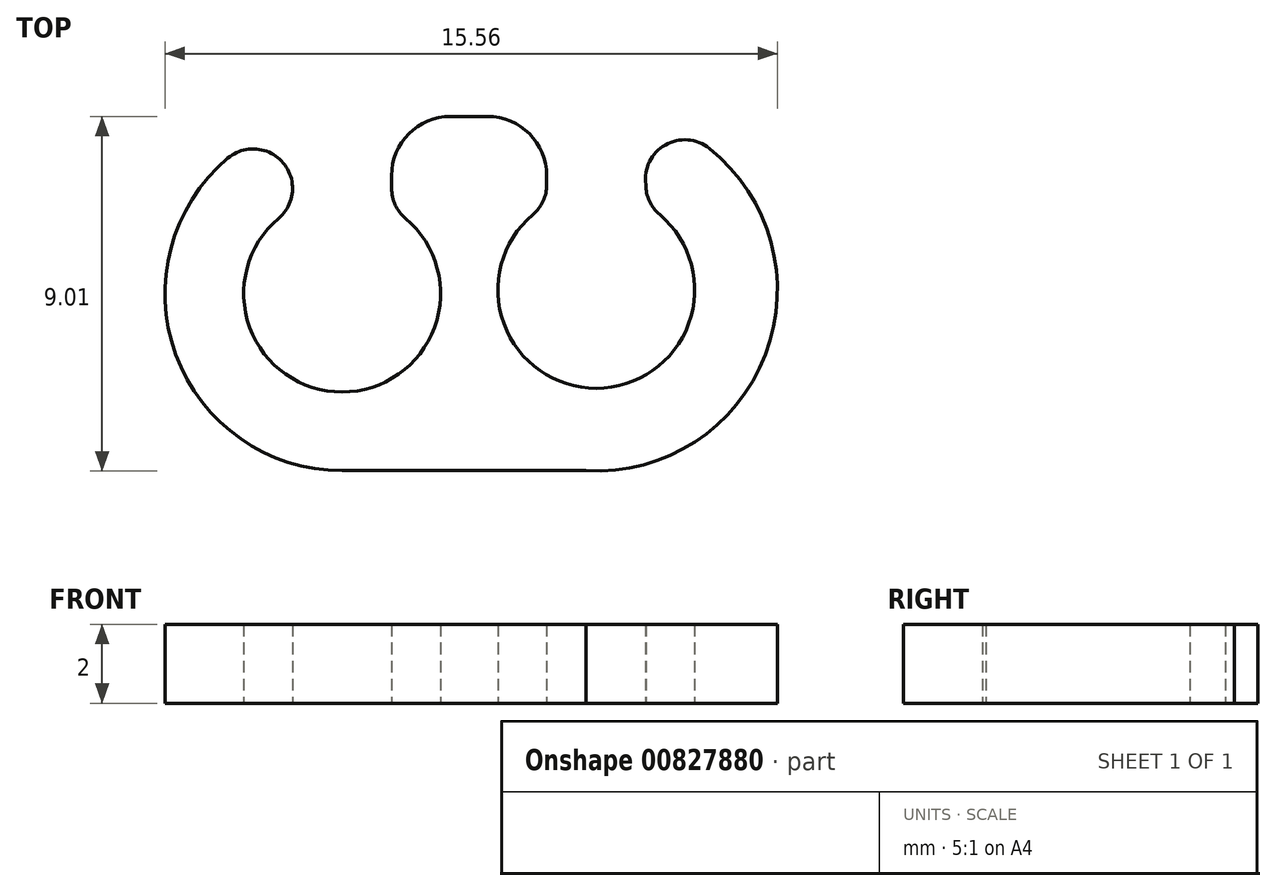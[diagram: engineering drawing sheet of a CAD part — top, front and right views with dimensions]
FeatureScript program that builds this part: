
annotation { "Feature Type Name" : "Feature", "Feature Type Description" : "" }
export const myFeature = defineFeature(function(context is Context, id is Id, definition is map)
    precondition{}
    {
        {
            var Q0;
            Q0=qCreatedBy(makeId("Top.planeOp"),FACE);
            var sketch = newSketch(context, id + "F0", { "sketchPlane" : qUnion([Q0])});
            skArc(sketch, "E0", {"start": v(-38.87, -11.61) * mm, "mid": v(-37.26, -16.02) * mm, "end": v(-35.65, -11.61) * mm});
            skArc(sketch, "E1.3.0.0", {"start": v(-32.41, -11.52) * mm, "mid": v(-30.8, -15.93) * mm, "end": v(-29.19, -11.52) * mm});
            skArc(sketch, "E2", {"start": v(-31.06, -18.02) * mm, "mid": v(-26.5, -15.07) * mm, "end": v(-27.93, -9.83) * mm});
            skArc(sketch, "E3", {"start": v(-40.16, -10.08) * mm, "mid": v(-41.49, -15.07) * mm, "end": v(-37.26, -18.02) * mm});
            skLineSegment(sketch, "E4", {"start": v(-34.5, -9.02) * mm, "end": v(-33.56, -9.02) * mm});
            skLineSegment(sketch, "E5.left", {"start": v(-36, -10.85) * mm, "end": v(-36, -10.52) * mm});
            skLineSegment(sketch, "E6.3.0.1", {"start": v(-32.06, -10.75) * mm, "end": v(-32.06, -10.52) * mm});
            skArc(sketch, "E7.filletArc", {"start": v(-38.87, -11.61) * mm, "mid": v(-38.61, -11.27) * mm, "end": v(-38.52, -10.85) * mm});
            skArc(sketch, "E8.filletArc", {"start": v(-36, -10.85) * mm, "mid": v(-35.9, -11.27) * mm, "end": v(-35.65, -11.61) * mm});
            skArc(sketch, "E9.filletArc", {"start": v(-38.52, -10.85) * mm, "mid": v(-39.1, -9.94) * mm, "end": v(-40.16, -10.08) * mm});
            skArc(sketch, "E10.filletArc", {"start": v(-27.93, -9.83) * mm, "mid": v(-29.05, -9.75) * mm, "end": v(-29.54, -10.75) * mm});
            skArc(sketch, "E11.filletArc", {"start": v(-29.54, -10.75) * mm, "mid": v(-29.45, -11.18) * mm, "end": v(-29.19, -11.52) * mm});
            skArc(sketch, "E12.filletArc", {"start": v(-32.41, -11.52) * mm, "mid": v(-32.15, -11.18) * mm, "end": v(-32.06, -10.75) * mm});
            skArc(sketch, "E13.filletArc", {"start": v(-34.5, -9.02) * mm, "mid": v(-35.56, -9.46) * mm, "end": v(-36, -10.52) * mm});
            skArc(sketch, "E14.filletArc", {"start": v(-32.06, -10.52) * mm, "mid": v(-32.5, -9.46) * mm, "end": v(-33.56, -9.02) * mm});
            skLineSegment(sketch, "E15", {"start": v(-37.26, -18.02) * mm, "end": v(-31.06, -18.02) * mm});
            skSolve(sketch);
        }
        {
            var Q0;
            Q0 = qSketchRegion(id + "F0", true);
            extrude(context, id + "F1", {"entities" : qUnion([Q0]), "depth" : 2 * mm, "offsetDistance" : 25 * mm});
        }
    });
